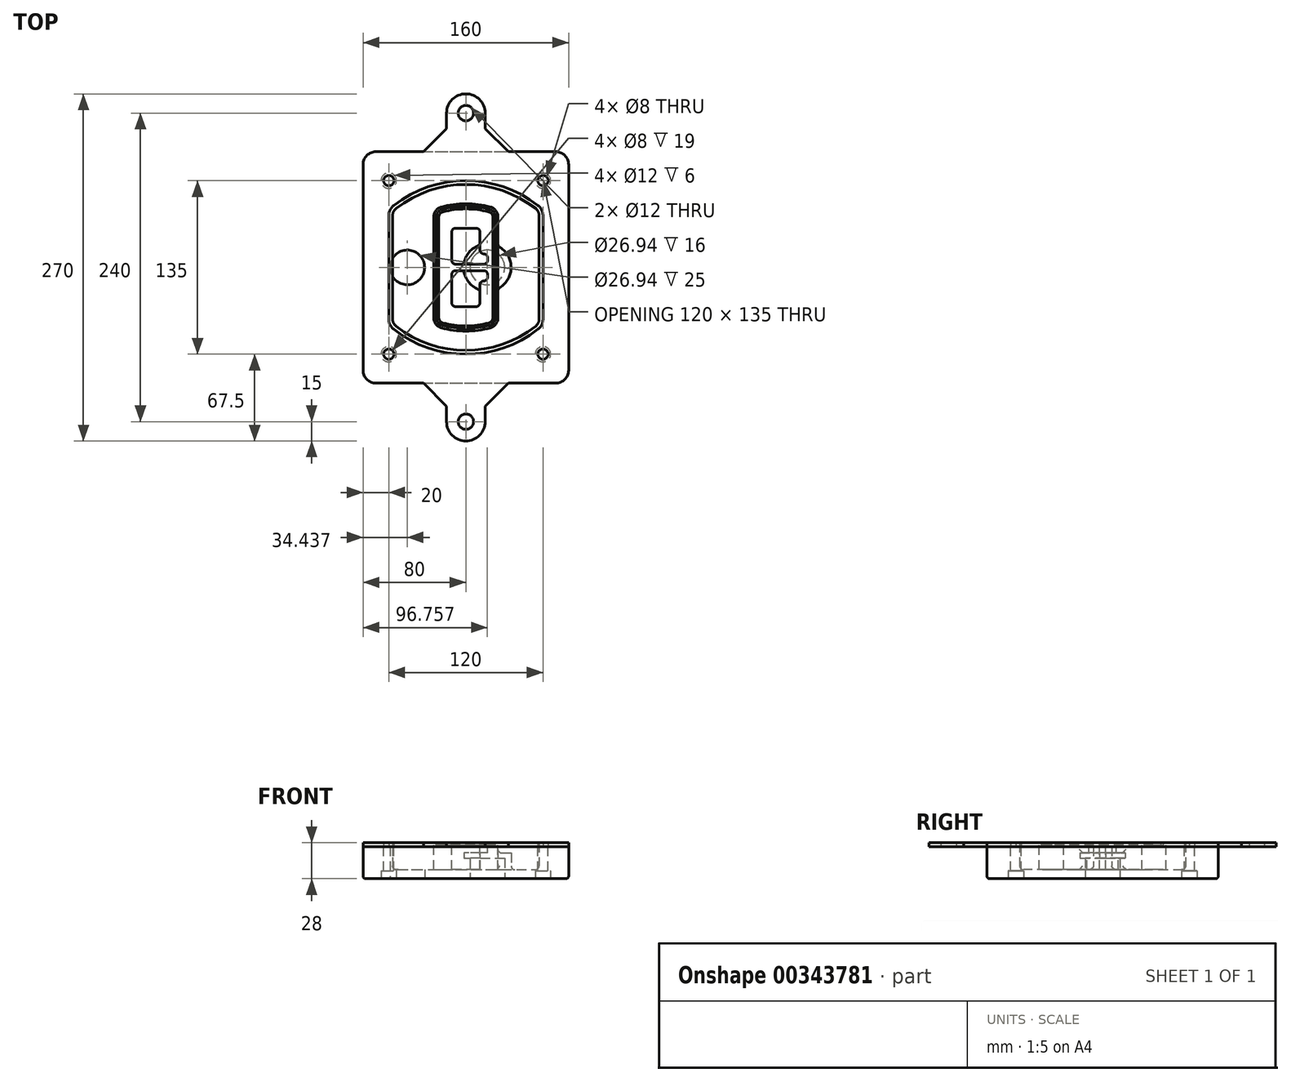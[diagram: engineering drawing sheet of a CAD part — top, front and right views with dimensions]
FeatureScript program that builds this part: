
annotation { "Feature Type Name" : "Feature", "Feature Type Description" : "" }
export const myFeature = defineFeature(function(context is Context, id is Id, definition is map)
    precondition{}
    {
        {
            var Q0;
            Q0=qCreatedBy(makeId("Top.planeOp"),FACE);
            var sketch = newSketch(context, id + "F0", { "sketchPlane" : qUnion([Q0])});
            skPoint(sketch, "E0.rect.middle", {"position": v(0, 0) * mm});
            skLineSegment(sketch, "E1.bottom", {"start": v(-70, -90) * mm, "end": v(70, -90) * mm});
            skLineSegment(sketch, "E1.top", {"start": v(-70, 90) * mm, "end": v(70, 90) * mm});
            skLineSegment(sketch, "E1.left", {"start": v(-80, -80) * mm, "end": v(-80, 80) * mm});
            skLineSegment(sketch, "E1.right", {"start": v(80, -80) * mm, "end": v(80, 80) * mm});
            skLineSegment(sketch, "E2", {"start": v(-80, 90) * mm, "end": v(80, -90) * mm, "construction": true});
            skLineSegment(sketch, "E3", {"start": v(80, 90) * mm, "end": v(-80, -90) * mm, "construction": true});
            skCircle(sketch, "E4", {"center": v(-60, 67.5) * mm, "radius": 4 * mm});
            skCircle(sketch, "E5", {"center": v(60, 67.5) * mm, "radius": 4 * mm});
            skCircle(sketch, "E6", {"center": v(60, -67.5) * mm, "radius": 4 * mm});
            skCircle(sketch, "E7", {"center": v(-60, -67.5) * mm, "radius": 4 * mm});
            skLineSegment(sketch, "E8", {"start": v(-60, 67.5) * mm, "end": v(60, 67.5) * mm, "construction": true});
            skLineSegment(sketch, "E9", {"start": v(60, 67.5) * mm, "end": v(60, -67.5) * mm, "construction": true});
            skLineSegment(sketch, "E10", {"start": v(60, -67.5) * mm, "end": v(-60, -67.5) * mm, "construction": true});
            skLineSegment(sketch, "E11", {"start": v(-60, -67.5) * mm, "end": v(-60, 67.5) * mm, "construction": true});
            skLineSegment(sketch, "E12", {"start": v(-60, 40.3) * mm, "end": v(-60, -40.3) * mm});
            skLineSegment(sketch, "E13", {"start": v(60, 40.3) * mm, "end": v(60, -40.3) * mm});
            skArc(sketch, "E14", {"start": v(56.15, 48.18) * mm, "mid": v(0, 67.5) * mm, "end": v(-56.15, 48.18) * mm});
            skArc(sketch, "E15", {"start": v(-56.15, -48.18) * mm, "mid": v(0, -67.5) * mm, "end": v(56.15, -48.18) * mm});
            skLineSegment(sketch, "E16", {"start": v(-60, 0) * mm, "end": v(60, 0) * mm, "construction": true});
            skPoint(sketch, "E17.visualSharp", {"position": v(-60, -45) * mm});
            skArc(sketch, "E17.filletArc", {"start": v(-60, -40.3) * mm, "mid": v(-58.99, -44.68) * mm, "end": v(-56.15, -48.18) * mm});
            skPoint(sketch, "E18.visualSharp", {"position": v(-60, 45) * mm});
            skArc(sketch, "E18.filletArc", {"start": v(-56.15, 48.18) * mm, "mid": v(-58.99, 44.68) * mm, "end": v(-60, 40.3) * mm});
            skPoint(sketch, "E19.visualSharp", {"position": v(60, 45) * mm});
            skArc(sketch, "E19.filletArc", {"start": v(60, 40.3) * mm, "mid": v(58.99, 44.68) * mm, "end": v(56.15, 48.18) * mm});
            skPoint(sketch, "E20.visualSharp", {"position": v(60, -45) * mm});
            skArc(sketch, "E20.filletArc", {"start": v(56.15, -48.18) * mm, "mid": v(58.99, -44.68) * mm, "end": v(60, -40.3) * mm});
            skPoint(sketch, "E21.visualSharp", {"position": v(-80, 90) * mm});
            skArc(sketch, "E21.filletArc", {"start": v(-70, 90) * mm, "mid": v(-77.07, 87.07) * mm, "end": v(-80, 80) * mm});
            skPoint(sketch, "E22.visualSharp", {"position": v(80, 90) * mm});
            skArc(sketch, "E22.filletArc", {"start": v(80, 80) * mm, "mid": v(77.07, 87.07) * mm, "end": v(70, 90) * mm});
            skPoint(sketch, "E23.visualSharp", {"position": v(80, -90) * mm});
            skArc(sketch, "E23.filletArc", {"start": v(70, -90) * mm, "mid": v(77.07, -87.07) * mm, "end": v(80, -80) * mm});
            skPoint(sketch, "E24.visualSharp", {"position": v(-80, -90) * mm});
            skArc(sketch, "E24.filletArc", {"start": v(-80, -80) * mm, "mid": v(-77.07, -87.07) * mm, "end": v(-70, -90) * mm});
            skArc(sketch, "E25.0", {"start": v(57, 40.3) * mm, "mid": v(56.3, 43.36) * mm, "end": v(54.3, 45.81) * mm});
            skLineSegment(sketch, "E25.1", {"start": v(57, 40.3) * mm, "end": v(57, -40.3) * mm});
            skArc(sketch, "E25.2", {"start": v(54.3, -45.81) * mm, "mid": v(56.3, -43.36) * mm, "end": v(57, -40.3) * mm});
            skArc(sketch, "E25.3", {"start": v(-54.3, -45.81) * mm, "mid": v(0, -64.5) * mm, "end": v(54.3, -45.81) * mm});
            skArc(sketch, "E25.4", {"start": v(-57, -40.3) * mm, "mid": v(-56.3, -43.36) * mm, "end": v(-54.3, -45.81) * mm});
            skArc(sketch, "E25.5", {"start": v(54.3, 45.81) * mm, "mid": v(0, 64.5) * mm, "end": v(-54.3, 45.81) * mm});
            skLineSegment(sketch, "E25.6", {"start": v(-57, 40.3) * mm, "end": v(-57, -40.3) * mm});
            skArc(sketch, "E25.7", {"start": v(-54.3, 45.81) * mm, "mid": v(-56.3, 43.36) * mm, "end": v(-57, 40.3) * mm});
            skArc(sketch, "E26.0", {"start": v(-58.62, 51.33) * mm, "mid": v(-62.58, 46.43) * mm, "end": v(-64, 40.3) * mm});
            skArc(sketch, "E26.1", {"start": v(58.62, 51.33) * mm, "mid": v(0, 71.5) * mm, "end": v(-58.62, 51.33) * mm});
            skArc(sketch, "E26.2", {"start": v(64, 40.3) * mm, "mid": v(62.58, 46.43) * mm, "end": v(58.62, 51.33) * mm});
            skLineSegment(sketch, "E26.3", {"start": v(64, 40.3) * mm, "end": v(64, -40.3) * mm});
            skArc(sketch, "E26.4", {"start": v(58.62, -51.33) * mm, "mid": v(62.58, -46.43) * mm, "end": v(64, -40.3) * mm});
            skLineSegment(sketch, "E26.5", {"start": v(-64, 40.3) * mm, "end": v(-64, -40.3) * mm});
            skArc(sketch, "E26.6", {"start": v(-58.62, -51.33) * mm, "mid": v(0, -71.5) * mm, "end": v(58.62, -51.33) * mm});
            skArc(sketch, "E26.7", {"start": v(-64, -40.3) * mm, "mid": v(-62.58, -46.43) * mm, "end": v(-58.62, -51.33) * mm});
            skSolve(sketch);
        }
        {
            var Q0;
            Q0=makeQuery(id+"F0.imprint","IMPRINT",FACE,{"disambiguationData":[TD([[makeQuery(id+"F0.imprint","IMPRINT",EDGE,{"derivedFrom":sQuery(id+"F0.wireOp",EDGE,"E1.bottom")}),1.0]])]});
            var Q1;
            Q1=makeQuery(id+"F0.imprint","IMPRINT",FACE,{"disambiguationData":[TD([[makeQuery(id+"F0.imprint","IMPRINT",EDGE,{"derivedFrom":sQuery(id+"F0.wireOp",EDGE,"E12")}),1.0]])]});
            var Q2;
            Q2=makeQuery(id+"F0.imprint","IMPRINT",FACE,{"disambiguationData":[TD([[makeQuery(id+"F0.imprint","IMPRINT",EDGE,{"derivedFrom":sQuery(id+"F0.wireOp",EDGE,"E25.0")}),1.0]])]});
            var Q3;
            Q3=makeQuery(id+"F0.imprint","IMPRINT",FACE,{"disambiguationData":[TD([[makeQuery(id+"F0.imprint","IMPRINT",EDGE,{"derivedFrom":sQuery(id+"F0.wireOp",EDGE,"E12")}),-1.0]])]});
            extrude(context, id + "F1", {"entities" : qUnion([Q0, Q1, Q2, Q3]), "oppositeDirection" : true, "depth" : 25 * mm});
        }
        {
            var Q0;
            Q0=makeQuery(id+"F0.imprint","IMPRINT",FACE,{"disambiguationData":[TD([[makeQuery(id+"F0.imprint","IMPRINT",EDGE,{"derivedFrom":sQuery(id+"F0.wireOp",EDGE,"E12")}),1.0]])]});
            extrude(context, id + "F2", {"entities" : qUnion([Q0]), "operationType" : NewBodyOperationType.ADD, "depth" : 3 * mm});
        }
        {
            var Q0;
            Q0=makeQuery(id+"F0.imprint","IMPRINT",FACE,{"disambiguationData":[TD([[makeQuery(id+"F0.imprint","IMPRINT",EDGE,{"derivedFrom":sQuery(id+"F0.wireOp",EDGE,"E25.0")}),1.0]])]});
            extrude(context, id + "F3", {"entities" : qUnion([Q0]), "operationType" : NewBodyOperationType.REMOVE, "oppositeDirection" : true, "depth" : 18 * mm});
        }
        {
            var Q0;
            Q0=makeQuery(id+"F2.opExtrude","CAP_FACE",FACE,{"disambiguationData":[OSD([sQuery(id+"F0.wireOp",EDGE,"E12"),sQuery(id+"F0.wireOp",EDGE,"E13"),sQuery(id+"F0.wireOp",EDGE,"E14"),sQuery(id+"F0.wireOp",EDGE,"E15"),sQuery(id+"F0.wireOp",EDGE,"E17.filletArc"),sQuery(id+"F0.wireOp",EDGE,"E18.filletArc"),sQuery(id+"F0.wireOp",EDGE,"E19.filletArc"),sQuery(id+"F0.wireOp",EDGE,"E20.filletArc"),sQuery(id+"F0.wireOp",EDGE,"E25.0"),sQuery(id+"F0.wireOp",EDGE,"E25.1"),sQuery(id+"F0.wireOp",EDGE,"E25.2"),sQuery(id+"F0.wireOp",EDGE,"E25.3"),sQuery(id+"F0.wireOp",EDGE,"E25.4"),sQuery(id+"F0.wireOp",EDGE,"E25.5"),sQuery(id+"F0.wireOp",EDGE,"E25.6"),sQuery(id+"F0.wireOp",EDGE,"E25.7")])],"isStart":false});
            var sketch = newSketch(context, id + "F4", { "sketchPlane" : qUnion([Q0])});
            skArc(sketch, "E27.0", {"start": v(-19.08, -46.97) * mm, "mid": v(0, -49.5) * mm, "end": v(19.08, -46.97) * mm});
            skArc(sketch, "E28.0", {"start": v(19.08, 46.97) * mm, "mid": v(0, 49.5) * mm, "end": v(-19.08, 46.97) * mm});
            skLineSegment(sketch, "E29", {"start": v(-25, 39.25) * mm, "end": v(-25, -39.25) * mm});
            skLineSegment(sketch, "E30", {"start": v(25, 39.25) * mm, "end": v(25, -39.25) * mm});
            skLineSegment(sketch, "E31", {"start": v(-25, 45.1) * mm, "end": v(25, 45.1) * mm, "construction": true});
            skLineSegment(sketch, "E32", {"start": v(-25, -45.1) * mm, "end": v(25, -45.1) * mm, "construction": true});
            skPoint(sketch, "E33.visualSharp", {"position": v(-25, 45.1) * mm});
            skArc(sketch, "E33.filletArc", {"start": v(-19.08, 46.97) * mm, "mid": v(-23.35, 44.11) * mm, "end": v(-25, 39.25) * mm});
            skPoint(sketch, "E34.visualSharp", {"position": v(25, 45.1) * mm});
            skArc(sketch, "E34.filletArc", {"start": v(25, 39.25) * mm, "mid": v(23.35, 44.11) * mm, "end": v(19.08, 46.97) * mm});
            skPoint(sketch, "E35.visualSharp", {"position": v(25, -45.1) * mm});
            skArc(sketch, "E35.filletArc", {"start": v(19.08, -46.97) * mm, "mid": v(23.35, -44.11) * mm, "end": v(25, -39.25) * mm});
            skPoint(sketch, "E36.visualSharp", {"position": v(-25, -45.1) * mm});
            skArc(sketch, "E36.filletArc", {"start": v(-25, -39.25) * mm, "mid": v(-23.35, -44.11) * mm, "end": v(-19.08, -46.97) * mm});
            skArc(sketch, "E37.0", {"start": v(54.3, 45.81) * mm, "mid": v(0, 64.5) * mm, "end": v(-54.3, 45.81) * mm});
            skArc(sketch, "E37.1", {"start": v(-54.3, 45.81) * mm, "mid": v(-56.3, 43.36) * mm, "end": v(-57, 40.3) * mm});
            skLineSegment(sketch, "E37.2", {"start": v(-57, 40.3) * mm, "end": v(-57, -40.3) * mm});
            skArc(sketch, "E37.3", {"start": v(-57, -40.3) * mm, "mid": v(-56.3, -43.36) * mm, "end": v(-54.3, -45.81) * mm});
            skArc(sketch, "E37.4", {"start": v(-54.3, -45.81) * mm, "mid": v(0, -64.5) * mm, "end": v(54.3, -45.81) * mm});
            skArc(sketch, "E37.5", {"start": v(54.3, -45.81) * mm, "mid": v(56.3, -43.36) * mm, "end": v(57, -40.3) * mm});
            skLineSegment(sketch, "E37.6", {"start": v(57, 40.3) * mm, "end": v(57, -40.3) * mm});
            skArc(sketch, "E37.7", {"start": v(57, 40.3) * mm, "mid": v(56.3, 43.36) * mm, "end": v(54.3, 45.81) * mm});
            skLineSegment(sketch, "E38.0", {"start": v(23, 39.25) * mm, "end": v(23, -39.25) * mm});
            skArc(sketch, "E38.1", {"start": v(18.56, -45.04) * mm, "mid": v(21.76, -42.9) * mm, "end": v(23, -39.25) * mm});
            skArc(sketch, "E38.2", {"start": v(-18.56, -45.04) * mm, "mid": v(0, -47.5) * mm, "end": v(18.56, -45.04) * mm});
            skArc(sketch, "E38.3", {"start": v(-23, -39.25) * mm, "mid": v(-21.76, -42.9) * mm, "end": v(-18.56, -45.04) * mm});
            skLineSegment(sketch, "E38.4", {"start": v(-23, 39.25) * mm, "end": v(-23, -39.25) * mm});
            skArc(sketch, "E38.5", {"start": v(23, 39.25) * mm, "mid": v(21.76, 42.9) * mm, "end": v(18.56, 45.04) * mm});
            skArc(sketch, "E38.6", {"start": v(-18.56, 45.04) * mm, "mid": v(-21.76, 42.9) * mm, "end": v(-23, 39.25) * mm});
            skArc(sketch, "E38.7", {"start": v(18.56, 45.04) * mm, "mid": v(0, 47.5) * mm, "end": v(-18.56, 45.04) * mm});
            skArc(sketch, "E39.0", {"start": v(21, 39.25) * mm, "mid": v(20.18, 41.68) * mm, "end": v(18.04, 43.1) * mm});
            skLineSegment(sketch, "E39.1", {"start": v(21, 39.25) * mm, "end": v(21, -39.25) * mm});
            skArc(sketch, "E39.2", {"start": v(18.04, -43.1) * mm, "mid": v(20.18, -41.68) * mm, "end": v(21, -39.25) * mm});
            skArc(sketch, "E39.3", {"start": v(-18.04, -43.1) * mm, "mid": v(0, -45.5) * mm, "end": v(18.04, -43.1) * mm});
            skArc(sketch, "E39.4", {"start": v(-21, -39.25) * mm, "mid": v(-20.18, -41.68) * mm, "end": v(-18.04, -43.1) * mm});
            skArc(sketch, "E39.5", {"start": v(18.04, 43.1) * mm, "mid": v(0, 45.5) * mm, "end": v(-18.04, 43.1) * mm});
            skLineSegment(sketch, "E39.6", {"start": v(-21, 39.25) * mm, "end": v(-21, -39.25) * mm});
            skArc(sketch, "E39.7", {"start": v(-18.04, 43.1) * mm, "mid": v(-20.18, 41.68) * mm, "end": v(-21, 39.25) * mm});
            skLineSegment(sketch, "E40", {"start": v(-25, 0) * mm, "end": v(25, 0) * mm, "construction": true});
            skLineSegment(sketch, "E41", {"start": v(-11, 5.5) * mm, "end": v(-11, 27.5) * mm});
            skLineSegment(sketch, "E42", {"start": v(-8, 30.5) * mm, "end": v(8, 30.5) * mm});
            skLineSegment(sketch, "E43", {"start": v(11, 27.5) * mm, "end": v(11, 13.5) * mm});
            skLineSegment(sketch, "E44", {"start": v(14, 10.5) * mm, "end": v(14, 10.5) * mm});
            skLineSegment(sketch, "E45", {"start": v(17, 7.5) * mm, "end": v(17, 5.5) * mm});
            skLineSegment(sketch, "E46", {"start": v(14, 2.5) * mm, "end": v(-8, 2.5) * mm});
            skPoint(sketch, "E47.visualSharp", {"position": v(-11, 30.5) * mm});
            skArc(sketch, "E47.filletArc", {"start": v(-8, 30.5) * mm, "mid": v(-10.12, 29.62) * mm, "end": v(-11, 27.5) * mm});
            skPoint(sketch, "E48.visualSharp", {"position": v(11, 30.5) * mm});
            skArc(sketch, "E48.filletArc", {"start": v(11, 27.5) * mm, "mid": v(10.12, 29.62) * mm, "end": v(8, 30.5) * mm});
            skPoint(sketch, "E49.visualSharp", {"position": v(11, 10.5) * mm});
            skArc(sketch, "E49.filletArc", {"start": v(11, 13.5) * mm, "mid": v(11.88, 11.38) * mm, "end": v(14, 10.5) * mm});
            skPoint(sketch, "E50.visualSharp", {"position": v(17, 10.5) * mm});
            skArc(sketch, "E50.filletArc", {"start": v(17, 7.5) * mm, "mid": v(16.12, 9.62) * mm, "end": v(14, 10.5) * mm});
            skPoint(sketch, "E51.visualSharp", {"position": v(17, 2.5) * mm});
            skArc(sketch, "E51.filletArc", {"start": v(14, 2.5) * mm, "mid": v(16.12, 3.38) * mm, "end": v(17, 5.5) * mm});
            skPoint(sketch, "E52.visualSharp", {"position": v(-11, 2.5) * mm});
            skArc(sketch, "E52.filletArc", {"start": v(-11, 5.5) * mm, "mid": v(-10.12, 3.38) * mm, "end": v(-8, 2.5) * mm});
            skLineSegment(sketch, "E53.0.MirrorCS", {"start": v(14, -2.5) * mm, "end": v(-8, -2.5) * mm});
            skArc(sketch, "E54.0.MirrorCS", {"start": v(-11, -5.5) * mm, "mid": v(-10.12, -3.38) * mm, "end": v(-8, -2.5) * mm});
            skLineSegment(sketch, "E55.0.MirrorCS", {"start": v(-11, -5.5) * mm, "end": v(-11, -27.5) * mm});
            skArc(sketch, "E56.0.MirrorCS", {"start": v(-8, -30.5) * mm, "mid": v(-10.12, -29.62) * mm, "end": v(-11, -27.5) * mm});
            skLineSegment(sketch, "E57.0.MirrorCS", {"start": v(-8, -30.5) * mm, "end": v(8, -30.5) * mm});
            skArc(sketch, "E58.0.MirrorCS", {"start": v(11, -27.5) * mm, "mid": v(10.12, -29.62) * mm, "end": v(8, -30.5) * mm});
            skLineSegment(sketch, "E59.0.MirrorCS", {"start": v(11, -27.5) * mm, "end": v(11, -13.5) * mm});
            skArc(sketch, "E60.0.MirrorCS", {"start": v(11, -13.5) * mm, "mid": v(11.88, -11.38) * mm, "end": v(14, -10.5) * mm});
            skArc(sketch, "E61.0.MirrorCS", {"start": v(17, -7.5) * mm, "mid": v(16.12, -9.62) * mm, "end": v(14, -10.5) * mm});
            skLineSegment(sketch, "E62.0.MirrorCS", {"start": v(17, -7.5) * mm, "end": v(17, -5.5) * mm});
            skArc(sketch, "E63.0.MirrorCS", {"start": v(14, -2.5) * mm, "mid": v(16.12, -3.38) * mm, "end": v(17, -5.5) * mm});
            skSolve(sketch);
        }
        {
            var Q0;
            Q0=makeQuery(id+"F4.imprint","IMPRINT",FACE,{"disambiguationData":[TD([[makeQuery(id+"F4.imprint","IMPRINT",EDGE,{"derivedFrom":sQuery(id+"F4.wireOp",EDGE,"E27.0")}),1.0]])]});
            var Q1;
            Q1=makeQuery(id+"F4.imprint","IMPRINT",FACE,{"disambiguationData":[TD([[makeQuery(id+"F4.imprint","IMPRINT",EDGE,{"derivedFrom":sQuery(id+"F4.wireOp",EDGE,"E38.0")}),-1.0]])]});
            var Q2;
            Q2=makeQuery(id+"F4.imprint","IMPRINT",FACE,{"disambiguationData":[TD([[makeQuery(id+"F4.imprint","IMPRINT",EDGE,{"derivedFrom":sQuery(id+"F4.wireOp",EDGE,"E39.0")}),1.0]])]});
            extrude(context, id + "F5", {"entities" : qUnion([Q0, Q1, Q2]), "operationType" : NewBodyOperationType.ADD, "endBound" : BoundingType.UP_TO_NEXT, "oppositeDirection" : true, "depth" : 25 * mm});
        }
        {
            var Q0;
            Q0=makeQuery(id+"F4.imprint","IMPRINT",FACE,{"disambiguationData":[TD([[makeQuery(id+"F4.imprint","IMPRINT",EDGE,{"derivedFrom":sQuery(id+"F4.wireOp",EDGE,"E38.0")}),-1.0]])]});
            extrude(context, id + "F6", {"entities" : qUnion([Q0]), "operationType" : NewBodyOperationType.REMOVE, "oppositeDirection" : true, "depth" : 2 * mm});
        }
        {
            var Q0;
            Q0=makeQuery(id+"F1.opExtrude","CAP_FACE",FACE,{"disambiguationData":[OSD([sQuery(id+"F0.wireOp",EDGE,"E1.bottom"),sQuery(id+"F0.wireOp",EDGE,"E1.top"),sQuery(id+"F0.wireOp",EDGE,"E1.left"),sQuery(id+"F0.wireOp",EDGE,"E1.right"),sQuery(id+"F0.wireOp",EDGE,"E4"),sQuery(id+"F0.wireOp",EDGE,"E5"),sQuery(id+"F0.wireOp",EDGE,"E6"),sQuery(id+"F0.wireOp",EDGE,"E7"),sQuery(id+"F0.wireOp",EDGE,"E21.filletArc"),sQuery(id+"F0.wireOp",EDGE,"E22.filletArc"),sQuery(id+"F0.wireOp",EDGE,"E23.filletArc"),sQuery(id+"F0.wireOp",EDGE,"E24.filletArc")])],"isStart":false});
            var sketch = newSketch(context, id + "F7", { "sketchPlane" : qUnion([Q0])});
            skCircle(sketch, "E64", {"center": v(16.76, 0) * mm, "radius": 13.47 * mm});
            skCircle(sketch, "E65", {"center": v(-45.56, 0) * mm, "radius": 13.47 * mm});
            skLineSegment(sketch, "E66", {"start": v(80, 0) * mm, "end": v(-80, 0) * mm});
            skCircle(sketch, "E67", {"center": v(16.76, 0) * mm, "radius": 18.47 * mm});
            skCircle(sketch, "E68", {"center": v(60, -67.5) * mm, "radius": 6 * mm});
            skCircle(sketch, "E69", {"center": v(-60, -67.5) * mm, "radius": 6 * mm});
            skCircle(sketch, "E70", {"center": v(-60, 67.5) * mm, "radius": 6 * mm});
            skCircle(sketch, "E71", {"center": v(60, 67.5) * mm, "radius": 6 * mm});
            skSolve(sketch);
        }
        {
            var Q0;
            {var subQ1=sQuery(id+"F7.wireOp",EDGE,"E66");var subQ4=sQuery(id+"F7.wireOp",EDGE,"E64");var subQ6=makeQuery(id+"F7.imprint","INTERSECT",VERTEX,{"disambiguationData":[OD(0.0)],"derivedFrom":[subQ4,subQ1]});Q0=makeQuery(id+"F7.imprint","IMPRINT",FACE,{"disambiguationData":[TD([[makeQuery(id+"F7.imprint","IMPRINT",EDGE,{"disambiguationData":[TD([[subQ6,-1.0]])],"derivedFrom":subQ4}),-1.0]])]});}
            var Q1;
            {var subQ0=sQuery(id+"F7.wireOp",EDGE,"E66");var subQ1=sQuery(id+"F7.wireOp",EDGE,"E64");var subQ3=makeQuery(id+"F7.imprint","INTERSECT",VERTEX,{"disambiguationData":[OD(0.0)],"derivedFrom":[subQ1,subQ0]});Q1=makeQuery(id+"F7.imprint","IMPRINT",FACE,{"disambiguationData":[TD([[makeQuery(id+"F7.imprint","IMPRINT",EDGE,{"disambiguationData":[TD([[subQ3,-1.0]])],"derivedFrom":subQ1}),1.0]])]});}
            var Q2;
            {var subQ0=sQuery(id+"F7.wireOp",EDGE,"E66");var subQ1=sQuery(id+"F7.wireOp",EDGE,"E64");var subQ3=makeQuery(id+"F7.imprint","INTERSECT",VERTEX,{"disambiguationData":[OD(0.0)],"derivedFrom":[subQ1,subQ0]});Q2=makeQuery(id+"F7.imprint","IMPRINT",FACE,{"disambiguationData":[TD([[makeQuery(id+"F7.imprint","IMPRINT",EDGE,{"disambiguationData":[TD([[subQ3,1.0]])],"derivedFrom":subQ1}),1.0]])]});}
            var Q3;
            {var subQ1=sQuery(id+"F7.wireOp",EDGE,"E66");var subQ4=sQuery(id+"F7.wireOp",EDGE,"E64");var subQ6=makeQuery(id+"F7.imprint","INTERSECT",VERTEX,{"disambiguationData":[OD(0.0)],"derivedFrom":[subQ4,subQ1]});Q3=makeQuery(id+"F7.imprint","IMPRINT",FACE,{"disambiguationData":[TD([[makeQuery(id+"F7.imprint","IMPRINT",EDGE,{"disambiguationData":[TD([[subQ6,1.0]])],"derivedFrom":subQ4}),-1.0]])]});}
            extrude(context, id + "F8", {"entities" : qUnion([Q0, Q1, Q2, Q3]), "operationType" : NewBodyOperationType.ADD, "oppositeDirection" : true, "depth" : 20 * mm});
        }
        {
            var Q0;
            {var subQ0=sQuery(id+"F7.wireOp",EDGE,"E66");var subQ1=sQuery(id+"F7.wireOp",EDGE,"E64");var subQ3=makeQuery(id+"F7.imprint","INTERSECT",VERTEX,{"disambiguationData":[OD(0.0)],"derivedFrom":[subQ1,subQ0]});Q0=makeQuery(id+"F7.imprint","IMPRINT",FACE,{"disambiguationData":[TD([[makeQuery(id+"F7.imprint","IMPRINT",EDGE,{"disambiguationData":[TD([[subQ3,-1.0]])],"derivedFrom":subQ1}),1.0]])]});}
            var Q1;
            {var subQ0=sQuery(id+"F7.wireOp",EDGE,"E66");var subQ1=sQuery(id+"F7.wireOp",EDGE,"E64");var subQ3=makeQuery(id+"F7.imprint","INTERSECT",VERTEX,{"disambiguationData":[OD(0.0)],"derivedFrom":[subQ1,subQ0]});Q1=makeQuery(id+"F7.imprint","IMPRINT",FACE,{"disambiguationData":[TD([[makeQuery(id+"F7.imprint","IMPRINT",EDGE,{"disambiguationData":[TD([[subQ3,1.0]])],"derivedFrom":subQ1}),1.0]])]});}
            extrude(context, id + "F9", {"entities" : qUnion([Q0, Q1]), "operationType" : NewBodyOperationType.REMOVE, "oppositeDirection" : true, "depth" : 16 * mm});
        }
        {
            var Q0;
            {var subQ0=sQuery(id+"F7.wireOp",EDGE,"E66");var subQ1=sQuery(id+"F7.wireOp",EDGE,"E65");var subQ3=makeQuery(id+"F7.imprint","INTERSECT",VERTEX,{"disambiguationData":[OD(0.0)],"derivedFrom":[subQ1,subQ0]});Q0=makeQuery(id+"F7.imprint","IMPRINT",FACE,{"disambiguationData":[TD([[makeQuery(id+"F7.imprint","IMPRINT",EDGE,{"disambiguationData":[TD([[subQ3,-1.0]])],"derivedFrom":subQ1}),1.0]])]});}
            var Q1;
            {var subQ0=sQuery(id+"F7.wireOp",EDGE,"E66");var subQ1=sQuery(id+"F7.wireOp",EDGE,"E65");var subQ3=makeQuery(id+"F7.imprint","INTERSECT",VERTEX,{"disambiguationData":[OD(0.0)],"derivedFrom":[subQ1,subQ0]});Q1=makeQuery(id+"F7.imprint","IMPRINT",FACE,{"disambiguationData":[TD([[makeQuery(id+"F7.imprint","IMPRINT",EDGE,{"disambiguationData":[TD([[subQ3,1.0]])],"derivedFrom":subQ1}),1.0]])]});}
            extrude(context, id + "F10", {"entities" : qUnion([Q0, Q1]), "operationType" : NewBodyOperationType.REMOVE, "oppositeDirection" : true, "depth" : 25 * mm});
        }
        {
            var Q0;
            Q0=makeQuery(id+"F7.imprint","IMPRINT",FACE,{"disambiguationData":[TD([[makeQuery(id+"F7.imprint","IMPRINT",EDGE,{"derivedFrom":sQuery(id+"F7.wireOp",EDGE,"E68")}),1.0]])]});
            var Q1;
            Q1=makeQuery(id+"F7.imprint","IMPRINT",FACE,{"disambiguationData":[TD([[makeQuery(id+"F7.imprint","IMPRINT",EDGE,{"derivedFrom":makeQuery(id+"F1.opExtrude","CAP_EDGE",EDGE,{"disambiguationData":[OSD([sQuery(id+"F0.wireOp",EDGE,"E5")])],"isStart":false})}),-1.0]])]});
            var Q2;
            Q2=makeQuery(id+"F7.imprint","IMPRINT",FACE,{"disambiguationData":[TD([[makeQuery(id+"F7.imprint","IMPRINT",EDGE,{"derivedFrom":sQuery(id+"F7.wireOp",EDGE,"E69")}),1.0]])]});
            var Q3;
            Q3=makeQuery(id+"F7.imprint","IMPRINT",FACE,{"disambiguationData":[TD([[makeQuery(id+"F7.imprint","IMPRINT",EDGE,{"derivedFrom":makeQuery(id+"F1.opExtrude","CAP_EDGE",EDGE,{"disambiguationData":[OSD([sQuery(id+"F0.wireOp",EDGE,"E4")])],"isStart":false})}),-1.0]])]});
            var Q4;
            Q4=makeQuery(id+"F7.imprint","IMPRINT",FACE,{"disambiguationData":[TD([[makeQuery(id+"F7.imprint","IMPRINT",EDGE,{"derivedFrom":sQuery(id+"F7.wireOp",EDGE,"E70")}),1.0]])]});
            var Q5;
            Q5=makeQuery(id+"F7.imprint","IMPRINT",FACE,{"disambiguationData":[TD([[makeQuery(id+"F7.imprint","IMPRINT",EDGE,{"derivedFrom":makeQuery(id+"F1.opExtrude","CAP_EDGE",EDGE,{"disambiguationData":[OSD([sQuery(id+"F0.wireOp",EDGE,"E7")])],"isStart":false})}),-1.0]])]});
            var Q6;
            Q6=makeQuery(id+"F7.imprint","IMPRINT",FACE,{"disambiguationData":[TD([[makeQuery(id+"F7.imprint","IMPRINT",EDGE,{"derivedFrom":sQuery(id+"F7.wireOp",EDGE,"E71")}),1.0]])]});
            var Q7;
            Q7=makeQuery(id+"F7.imprint","IMPRINT",FACE,{"disambiguationData":[TD([[makeQuery(id+"F7.imprint","IMPRINT",EDGE,{"derivedFrom":makeQuery(id+"F1.opExtrude","CAP_EDGE",EDGE,{"disambiguationData":[OSD([sQuery(id+"F0.wireOp",EDGE,"E6")])],"isStart":false})}),-1.0]])]});
            extrude(context, id + "F11", {"entities" : qUnion([Q0, Q1, Q2, Q3, Q4, Q5, Q6, Q7]), "operationType" : NewBodyOperationType.REMOVE, "oppositeDirection" : true, "depth" : 6 * mm});
        }
        {
            var Q0;
            Q0=makeQuery(id+"F9.boolean.opBoolean","COPY",FACE,{"derivedFrom":makeQuery(id+"F9.opExtrude","CAP_FACE",FACE,{"disambiguationData":[OSD([sQuery(id+"F7.wireOp",EDGE,"E64")])],"isStart":false})});
            var sketch = newSketch(context, id + "F12", { "sketchPlane" : qUnion([Q0])});
            skArc(sketch, "E72.0", {"start": v(11, 17.55) * mm, "mid": v(2.57, 11.82) * mm, "end": v(-1.54, 2.5) * mm});
            skArc(sketch, "E72.1", {"start": v(-1.54, -2.5) * mm, "mid": v(2.57, -11.82) * mm, "end": v(11, -17.55) * mm});
            skLineSegment(sketch, "E73", {"start": v(-1.54, -2.5) * mm, "end": v(14, -2.5) * mm});
            skLineSegment(sketch, "E74.0", {"start": v(14, 2.5) * mm, "end": v(-1.54, 2.5) * mm});
            skArc(sketch, "E74.1", {"start": v(14, 2.5) * mm, "mid": v(16.12, 3.38) * mm, "end": v(17, 5.5) * mm});
            skLineSegment(sketch, "E74.2", {"start": v(17, 7.5) * mm, "end": v(17, 5.5) * mm});
            skArc(sketch, "E74.3", {"start": v(17, 7.5) * mm, "mid": v(16.12, 9.62) * mm, "end": v(14, 10.5) * mm});
            skArc(sketch, "E74.4", {"start": v(11, 13.5) * mm, "mid": v(11.88, 11.38) * mm, "end": v(14, 10.5) * mm});
            skLineSegment(sketch, "E74.5", {"start": v(11, 17.55) * mm, "end": v(11, 13.5) * mm});
            skLineSegment(sketch, "E74.7", {"start": v(14, -2.5) * mm, "end": v(-1.54, -2.5) * mm});
            skArc(sketch, "E74.8", {"start": v(14, -2.5) * mm, "mid": v(16.12, -3.38) * mm, "end": v(17, -5.5) * mm});
            skLineSegment(sketch, "E74.9", {"start": v(17, -7.5) * mm, "end": v(17, -5.5) * mm});
            skArc(sketch, "E74.10", {"start": v(17, -7.5) * mm, "mid": v(16.12, -9.62) * mm, "end": v(14, -10.5) * mm});
            skArc(sketch, "E74.11", {"start": v(11, -13.5) * mm, "mid": v(11.88, -11.38) * mm, "end": v(14, -10.5) * mm});
            skLineSegment(sketch, "E74.12", {"start": v(11, -17.55) * mm, "end": v(11, -13.5) * mm});
            skPoint(sketch, "E75.orphan", {"position": v(11, -27.5) * mm});
            skPoint(sketch, "E76.orphan", {"position": v(-8, -2.5) * mm});
            skPoint(sketch, "E77.orphan", {"position": v(-8, 2.5) * mm});
            skPoint(sketch, "E78.orphan", {"position": v(11, 27.5) * mm});
            skSolve(sketch);
        }
        {
            var Q0;
            {var subQ7=sQuery(id+"F12.wireOp",EDGE,"E72.0");var subQ14=sQuery(id+"F12.wireOp",EDGE,"E72.1");var subQ16=sQuery(id+"F12.wireOp",EDGE,"E74.1");var subQ18=sQuery(id+"F12.wireOp",EDGE,"E74.8");Q0=qUnion([makeQuery(id+"F12.imprint","IMPRINT",FACE,{"disambiguationData":[TD([[makeQuery(id+"F12.imprint","IMPRINT",EDGE,{"derivedFrom":subQ7}),1.0]])]}),makeQuery(id+"F12.imprint","IMPRINT",FACE,{"disambiguationData":[TD([[makeQuery(id+"F12.imprint","IMPRINT",EDGE,{"derivedFrom":subQ14}),1.0]])]}),makeQuery(id+"F12.imprint","IMPRINT",FACE,{"disambiguationData":[TD([[makeQuery(id+"F12.imprint","IMPRINT",EDGE,{"derivedFrom":subQ16}),1.0]])]}),makeQuery(id+"F12.imprint","IMPRINT",FACE,{"disambiguationData":[TD([[makeQuery(id+"F12.imprint","IMPRINT",EDGE,{"derivedFrom":subQ18}),-1.0]])]})]);}
            var Q1;
            Q1=makeQuery(id+"F5.boolean.opBoolean","SPLIT",FACE,{"disambiguationData":[TD([makeQuery(id+"F5.opExtrude","SWEPT_FACE",FACE,{"disambiguationData":[OSD([sQuery(id+"F4.wireOp",EDGE,"E41")])]})])],"derivedFrom":makeQuery(id+"F3.boolean.opBoolean","COPY",FACE,{"derivedFrom":makeQuery(id+"F3.opExtrude","CAP_FACE",FACE,{"disambiguationData":[OSD([sQuery(id+"F0.wireOp",EDGE,"E25.0"),sQuery(id+"F0.wireOp",EDGE,"E25.1"),sQuery(id+"F0.wireOp",EDGE,"E25.2"),sQuery(id+"F0.wireOp",EDGE,"E25.3"),sQuery(id+"F0.wireOp",EDGE,"E25.4"),sQuery(id+"F0.wireOp",EDGE,"E25.5"),sQuery(id+"F0.wireOp",EDGE,"E25.6"),sQuery(id+"F0.wireOp",EDGE,"E25.7")])],"isStart":false})})});
            extrude(context, id + "F13", {"entities" : qUnion([Q0]), "operationType" : NewBodyOperationType.REMOVE, "endBound" : BoundingType.UP_TO_SURFACE, "endBoundEntityFace" : qUnion([Q1]), "depth" : 25 * mm});
        }
        {
            var Q0;
            Q0=makeQuery(id+"F3.boolean.opBoolean","COPY",EDGE,{"derivedFrom":makeQuery(id+"F3.opExtrude","CAP_EDGE",EDGE,{"disambiguationData":[OSD([sQuery(id+"F0.wireOp",EDGE,"E25.6")])],"isStart":false})});
            var Q1;
            Q1=makeQuery(id+"F8.boolean.opBoolean","INTERSECT",EDGE,{"derivedFrom":[makeQuery(id+"F5.opExtrude","SWEPT_FACE",FACE,{"disambiguationData":[OSD([sQuery(id+"F4.wireOp",EDGE,"E30")])]}),makeQuery(id+"F8.opExtrude","CAP_FACE",FACE,{"disambiguationData":[OSD([sQuery(id+"F7.wireOp",EDGE,"E67")])],"isStart":false})]});
            var Q2;
            Q2=makeQuery(id+"F8.boolean.opBoolean","INTERSECT",EDGE,{"disambiguationData":[OD(1.0)],"derivedFrom":[makeQuery(id+"F5.opExtrude","SWEPT_FACE",FACE,{"disambiguationData":[OSD([sQuery(id+"F4.wireOp",EDGE,"E30")])]}),makeQuery(id+"F8.opExtrude","SWEPT_FACE",FACE,{"disambiguationData":[OSD([sQuery(id+"F7.wireOp",EDGE,"E67")])]})]});
            var Q3;
            {var subQ0=makeQuery(id+"F3.boolean.opBoolean","COPY",FACE,{"derivedFrom":makeQuery(id+"F3.opExtrude","CAP_FACE",FACE,{"disambiguationData":[OSD([sQuery(id+"F0.wireOp",EDGE,"E25.0"),sQuery(id+"F0.wireOp",EDGE,"E25.1"),sQuery(id+"F0.wireOp",EDGE,"E25.2"),sQuery(id+"F0.wireOp",EDGE,"E25.3"),sQuery(id+"F0.wireOp",EDGE,"E25.4"),sQuery(id+"F0.wireOp",EDGE,"E25.5"),sQuery(id+"F0.wireOp",EDGE,"E25.6"),sQuery(id+"F0.wireOp",EDGE,"E25.7")])],"isStart":false})});var subQ1=sQuery(id+"F4.wireOp",EDGE,"E30");Q3=makeQuery(id+"F8.boolean.opBoolean","SPLIT",EDGE,{"disambiguationData":[TD([makeQuery(id+"F5.opExtrude","SWEPT_FACE",FACE,{"disambiguationData":[OSD([sQuery(id+"F4.wireOp",EDGE,"E35.filletArc")])]})])],"derivedFrom":makeQuery(id+"F5.opExtrude","TWEAK_EDGE",EDGE,{"derivedFrom":[subQ0,makeQuery(id+"F4.imprint","IMPRINT",EDGE,{"derivedFrom":subQ1})]})});}
            var Q4;
            {var subQ0=sQuery(id+"F0.wireOp",EDGE,"E25.0");var subQ1=sQuery(id+"F0.wireOp",EDGE,"E25.1");var subQ2=sQuery(id+"F0.wireOp",EDGE,"E25.2");var subQ3=sQuery(id+"F0.wireOp",EDGE,"E25.3");var subQ4=sQuery(id+"F0.wireOp",EDGE,"E25.4");var subQ5=sQuery(id+"F0.wireOp",EDGE,"E25.5");var subQ6=sQuery(id+"F0.wireOp",EDGE,"E25.6");var subQ7=sQuery(id+"F0.wireOp",EDGE,"E25.7");Q4=makeQuery(id+"F8.boolean.opBoolean","INTERSECT",EDGE,{"derivedFrom":[makeQuery(id+"F5.boolean.opBoolean","SPLIT",FACE,{"disambiguationData":[TD([makeQuery(id+"F2.opExtrude","SWEPT_FACE",FACE,{"disambiguationData":[OSD([subQ0])]})])],"derivedFrom":makeQuery(id+"F3.boolean.opBoolean","COPY",FACE,{"derivedFrom":makeQuery(id+"F3.opExtrude","CAP_FACE",FACE,{"disambiguationData":[OSD([subQ0,subQ1,subQ2,subQ3,subQ4,subQ5,subQ6,subQ7])],"isStart":false})})}),makeQuery(id+"F8.opExtrude","SWEPT_FACE",FACE,{"disambiguationData":[OSD([sQuery(id+"F7.wireOp",EDGE,"E67")])]})]});}
            var Q5;
            Q5=makeQuery(id+"F8.boolean.opBoolean","INTERSECT",EDGE,{"disambiguationData":[OD(0.0)],"derivedFrom":[makeQuery(id+"F5.opExtrude","SWEPT_FACE",FACE,{"disambiguationData":[OSD([sQuery(id+"F4.wireOp",EDGE,"E30")])]}),makeQuery(id+"F8.opExtrude","SWEPT_FACE",FACE,{"disambiguationData":[OSD([sQuery(id+"F7.wireOp",EDGE,"E67")])]})]});
            fillet(context, id + "F14", {"entities" : qUnion([Q0, Q1, Q2, Q3, Q4, Q5]), "radius" : 3 * mm, "tangentPropagation" : true, "allowEdgeOverflow" : false});
        }
        {
            var Q0;
            Q0=makeQuery(id+"F1.opExtrude","CAP_EDGE",EDGE,{"disambiguationData":[OSD([sQuery(id+"F0.wireOp",EDGE,"E1.bottom")])],"isStart":false});
            fillet(context, id + "F15", {"entities" : qUnion([Q0]), "radius" : 2 * mm, "tangentPropagation" : true, "allowEdgeOverflow" : false});
        }
        {
            var Q0;
            {var subQ0=sQuery(id+"F0.wireOp",EDGE,"E21.filletArc");var subQ1=sQuery(id+"F0.wireOp",EDGE,"E7");var subQ2=sQuery(id+"F0.wireOp",EDGE,"E6");var subQ3=sQuery(id+"F0.wireOp",EDGE,"E5");var subQ4=sQuery(id+"F0.wireOp",EDGE,"E4");var subQ5=sQuery(id+"F0.wireOp",EDGE,"E22.filletArc");var subQ6=sQuery(id+"F0.wireOp",EDGE,"E1.bottom");var subQ7=sQuery(id+"F0.wireOp",EDGE,"E1.right");var subQ8=sQuery(id+"F0.wireOp",EDGE,"E1.top");var subQ9=sQuery(id+"F0.wireOp",EDGE,"E1.left");var subQ10=sQuery(id+"F0.wireOp",EDGE,"E23.filletArc");var subQ11=sQuery(id+"F0.wireOp",EDGE,"E24.filletArc");Q0=makeQuery(id+"F2.boolean.opBoolean","SPLIT",FACE,{"disambiguationData":[TD([makeQuery(id+"F1.opExtrude","SWEPT_FACE",FACE,{"disambiguationData":[OSD([subQ6])]})])],"derivedFrom":makeQuery(id+"F1.opExtrude","CAP_FACE",FACE,{"disambiguationData":[OSD([subQ6,subQ8,subQ9,subQ7,subQ4,subQ3,subQ2,subQ1,subQ0,subQ5,subQ10,subQ11])],"isStart":true})});}
            var sketch = newSketch(context, id + "F16", { "sketchPlane" : qUnion([Q0])});
            skPoint(sketch, "E79.endSnap0", {"position": v(0, 90) * mm});
            skLineSegment(sketch, "E80", {"start": v(0, 90) * mm, "end": v(0, 120) * mm, "construction": true});
            skCircle(sketch, "E81", {"center": v(0, 120) * mm, "radius": 6 * mm});
            skArc(sketch, "E82", {"start": v(15, 120) * mm, "mid": v(0, 135) * mm, "end": v(-15, 120) * mm});
            skLineSegment(sketch, "E83", {"start": v(-15, 120) * mm, "end": v(-15, 108) * mm});
            skLineSegment(sketch, "E84", {"start": v(-15, 108) * mm, "end": v(-33, 90) * mm});
            skLineSegment(sketch, "E85", {"start": v(15, 120) * mm, "end": v(15, 108) * mm});
            skLineSegment(sketch, "E86", {"start": v(15, 108) * mm, "end": v(33, 90) * mm});
            skLineSegment(sketch, "E87", {"start": v(-80, 0) * mm, "end": v(80, 0) * mm, "construction": true});
            skArc(sketch, "E88.MirrorCS", {"start": v(-15, 120) * mm, "mid": v(0, 135) * mm, "end": v(15, 120) * mm});
            skLineSegment(sketch, "E89.MirrorCS", {"start": v(-15, -120) * mm, "end": v(-15, -108) * mm});
            skLineSegment(sketch, "E90.MirrorCS", {"start": v(15, -120) * mm, "end": v(15, -108) * mm});
            skPoint(sketch, "E91.MirrorP", {"position": v(0, -90) * mm});
            skLineSegment(sketch, "E92.MirrorCS", {"start": v(-15, -108) * mm, "end": v(-33, -90) * mm});
            skCircle(sketch, "E93.MirrorC", {"center": v(0, -120) * mm, "radius": 6 * mm});
            skArc(sketch, "E94.MirrorCS", {"start": v(15, -120) * mm, "mid": v(0, -135) * mm, "end": v(-15, -120) * mm});
            skLineSegment(sketch, "E95.MirrorCS", {"start": v(15, -108) * mm, "end": v(33, -90) * mm});
            skArc(sketch, "E96.MirrorCS", {"start": v(-15, -120) * mm, "mid": v(0, -135) * mm, "end": v(15, -120) * mm});
            skLineSegment(sketch, "E97.MirrorCS", {"start": v(0, -90) * mm, "end": v(0, -120) * mm, "construction": true});
            skSolve(sketch);
        }
        {
            var Q0;
            Q0=makeQuery(id+"F16.imprint","IMPRINT",FACE,{"disambiguationData":[TD([[makeQuery(id+"F16.imprint","IMPRINT",EDGE,{"derivedFrom":sQuery(id+"F16.wireOp",EDGE,"E89.MirrorCS")}),-1.0]])]});
            var Q1;
            Q1=makeQuery(id+"F16.imprint","IMPRINT",FACE,{"disambiguationData":[TD([[makeQuery(id+"F16.imprint","IMPRINT",EDGE,{"derivedFrom":sQuery(id+"F16.wireOp",EDGE,"E83")}),1.0]])]});
            var Q2;
            Q2=makeQuery(id+"F16.imprint","IMPRINT",FACE,{"disambiguationData":[TD([[makeQuery(id+"F16.imprint","IMPRINT",EDGE,{"derivedFrom":makeQuery(id+"F1.opExtrude","CAP_EDGE",EDGE,{"disambiguationData":[OSD([sQuery(id+"F0.wireOp",EDGE,"E1.left")])],"isStart":true})}),-1.0]])]});
            var Q3;
            Q3=makeQuery(id+"F2.opExtrude","CAP_FACE",FACE,{"disambiguationData":[OSD([sQuery(id+"F0.wireOp",EDGE,"E12"),sQuery(id+"F0.wireOp",EDGE,"E13"),sQuery(id+"F0.wireOp",EDGE,"E14"),sQuery(id+"F0.wireOp",EDGE,"E15"),sQuery(id+"F0.wireOp",EDGE,"E17.filletArc"),sQuery(id+"F0.wireOp",EDGE,"E18.filletArc"),sQuery(id+"F0.wireOp",EDGE,"E19.filletArc"),sQuery(id+"F0.wireOp",EDGE,"E20.filletArc"),sQuery(id+"F0.wireOp",EDGE,"E25.0"),sQuery(id+"F0.wireOp",EDGE,"E25.1"),sQuery(id+"F0.wireOp",EDGE,"E25.2"),sQuery(id+"F0.wireOp",EDGE,"E25.3"),sQuery(id+"F0.wireOp",EDGE,"E25.4"),sQuery(id+"F0.wireOp",EDGE,"E25.5"),sQuery(id+"F0.wireOp",EDGE,"E25.6"),sQuery(id+"F0.wireOp",EDGE,"E25.7")])],"isStart":false});
            extrude(context, id + "F17", {"entities" : qUnion([Q0, Q1, Q2]), "endBound" : BoundingType.UP_TO_SURFACE, "endBoundEntityFace" : qUnion([Q3]), "depth" : 25 * mm});
        }
    });
